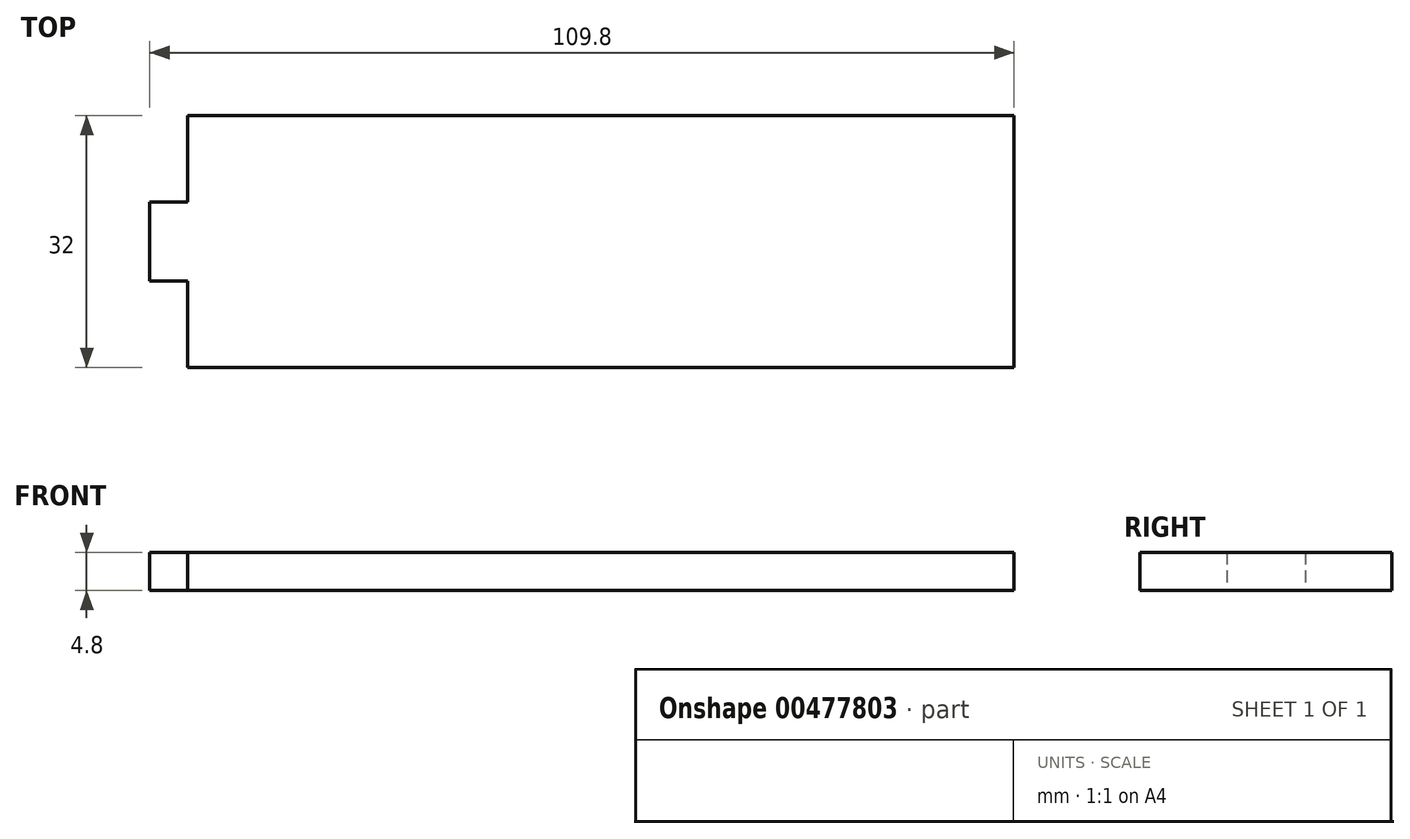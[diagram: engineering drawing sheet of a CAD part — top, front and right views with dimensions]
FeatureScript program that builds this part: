
annotation { "Feature Type Name" : "Feature", "Feature Type Description" : "" }
export const myFeature = defineFeature(function(context is Context, id is Id, definition is map)
    precondition{}
    {
        {
            var Q0;
            Q0=qCreatedBy(makeId("Top.planeOp"),FACE);
            var sketch = newSketch(context, id + "F0", { "sketchPlane" : qUnion([Q0])});
            skLineSegment(sketch, "E0.bottom", {"start": v(0, 0) * mm, "end": v(105, 0) * mm});
            skLineSegment(sketch, "E0.top", {"start": v(0, 32) * mm, "end": v(105, 32) * mm});
            skLineSegment(sketch, "E0.left", {"start": v(0, 0) * mm, "end": v(0, 32) * mm});
            skLineSegment(sketch, "E0.right", {"start": v(105, 0) * mm, "end": v(105, 32) * mm});
            skLineSegment(sketch, "E1.bottom", {"start": v(0, 21) * mm, "end": v(-4.8, 21) * mm});
            skLineSegment(sketch, "E1.top", {"start": v(0, 11) * mm, "end": v(-4.8, 11) * mm});
            skLineSegment(sketch, "E1.left", {"start": v(0, 21) * mm, "end": v(0, 11) * mm});
            skLineSegment(sketch, "E1.right", {"start": v(-4.8, 21) * mm, "end": v(-4.8, 11) * mm});
            skSolve(sketch);
        }
        {
            var Q0;
            Q0=qSketchRegion(id+"F0",true);
            extrude(context, id + "F1", {"entities" : qUnion([Q0]), "depth" : 4.8 * mm});
        }
    });
